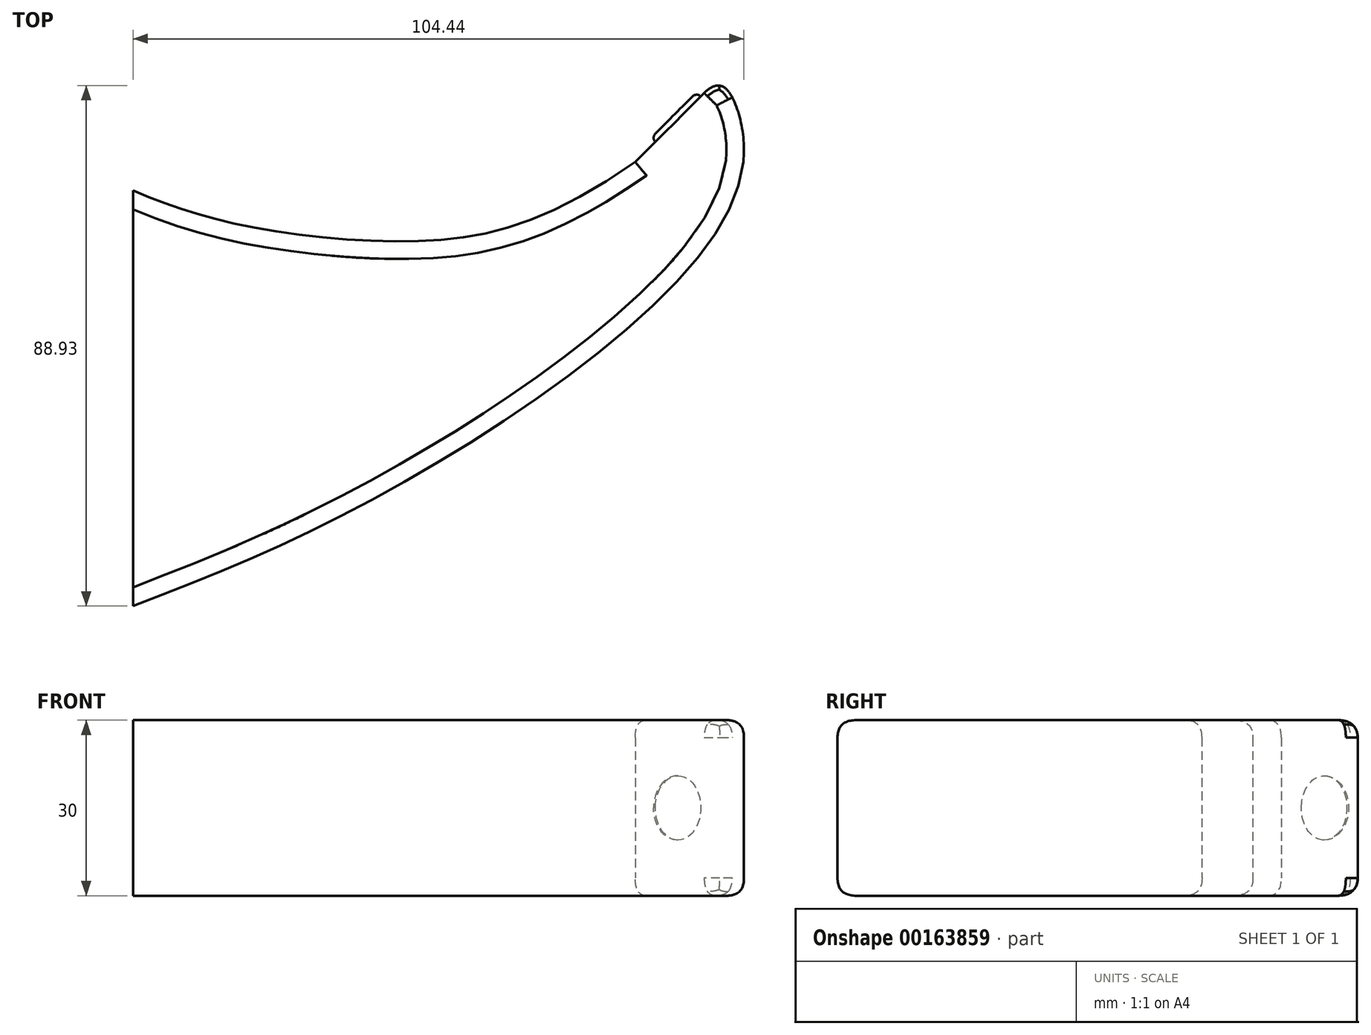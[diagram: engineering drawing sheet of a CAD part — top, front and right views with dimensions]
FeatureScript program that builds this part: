
annotation { "Feature Type Name" : "Feature", "Feature Type Description" : "" }
export const myFeature = defineFeature(function(context is Context, id is Id, definition is map)
    precondition{}
    {
        {
            var Q0;
            Q0=qCreatedBy(makeId("Top.planeOp"),FACE);
            var sketch = newSketch(context, id + "F0", { "sketchPlane" : qUnion([Q0])});
            skLineSegment(sketch, "E0", {"start": v(20.08, 24.8) * mm, "end": v(34.22, 38.94) * mm});
            skLineSegment(sketch, "E1", {"start": v(20.08, 24.8) * mm, "end": v(38.55, 24.8) * mm});
            skLineSegment(sketch, "E2", {"start": v(-65.78, -51.06) * mm, "end": v(-65.78, 48.94) * mm});
            skLineSegment(sketch, "E3", {"start": v(-65.78, -26.25) * mm, "end": v(-65.78, 19.94) * mm});
            skFitSpline(sketch, "E4", {"points": [v(-65.78, 19.94) * mm, v(-48.1, 14.22) * mm, v(-16.48, 11.31) * mm, v(20.08, 24.8) * mm], "startDerivative": vector(62.46, -26.54) * mm, "endDerivative": vector(118.27, 81.8) * mm});
            skFitSpline(sketch, "E5", {"points": [v(-65.78, -51.06) * mm, v(-27.67, -34.37) * mm, v(20.08, -2.5) * mm, v(38.55, 24.8) * mm, v(34.22, 38.94) * mm], "startDerivative": vector(142.55, 54.06) * mm, "endDerivative": vector(-50.17, 36.42) * mm});
            skLineSegment(sketch, "E6", {"start": v(34.22, 38.94) * mm, "end": v(-65.78, 38.94) * mm});
            skSolve(sketch);
        }
        {
            var Q0;
            {var subQ4=sQuery(id+"F0.wireOp",EDGE,"E1");Q0=makeQuery(id+"F0.imprint","IMPRINT",FACE,{"disambiguationData":[TD([[makeQuery(id+"F0.imprint","IMPRINT",EDGE,{"derivedFrom":subQ4}),-1.0]])]});}
            var Q1;
            {var subQ0=sQuery(id+"F0.wireOp",EDGE,"E0");Q1=makeQuery(id+"F0.imprint","IMPRINT",FACE,{"disambiguationData":[TD([[makeQuery(id+"F0.imprint","IMPRINT",EDGE,{"derivedFrom":subQ0}),-1.0]])]});}
            extrude(context, id + "F1", {"entities" : qUnion([Q0, Q1]), "endBound" : BoundingType.SYMMETRIC, "depth" : 30 * mm});
        }
        {
            var Q0;
            Q0=makeQuery(id+"F1.opExtrude","SWEPT_FACE",FACE,{"disambiguationData":[OSD([sQuery(id+"F0.wireOp",EDGE,"E0")])]});
            var sketch = newSketch(context, id + "F2", { "sketchPlane" : qUnion([Q0])});
            skCircle(sketch, "E7", {"center": v(-42.08, 0) * mm, "radius": 5.5 * mm});
            skSolve(sketch);
        }
        {
            var Q0;
            Q0=makeQuery(id+"F2.imprint","IMPRINT",FACE,{"disambiguationData":[TD([[makeQuery(id+"F2.imprint","IMPRINT",EDGE,{"derivedFrom":sQuery(id+"F2.wireOp",EDGE,"E7")}),1.0]])]});
            extrude(context, id + "F3", {"entities" : qUnion([Q0]), "operationType" : NewBodyOperationType.ADD, "depth" : 1 * mm});
        }
        {
            var Q0;
            Q0=makeQuery(id+"F3.opExtrude","CAP_FACE",FACE,{"disambiguationData":[OSD([sQuery(id+"F2.wireOp",EDGE,"E7")])],"isStart":false});
            fillet(context, id + "F4", {"entities" : qUnion([Q0]), "radius" : 1 * mm, "tangentPropagation" : true, "allowEdgeOverflow" : false});
        }
        {
            var Q0;
            Q0=makeQuery(id+"F1.opExtrude","SWEPT_EDGE",EDGE,{"disambiguationData":[OSD([sQuery(id+"F0.wireOp",EDGE,"E0"),sQuery(id+"F0.wireOp",EDGE,"E5"),sQuery(id+"F0.wireOp",EDGE,"E6")])]});
            var Q1;
            Q1=makeQuery(id+"F1.opExtrude","CAP_EDGE",EDGE,{"disambiguationData":[OSD([sQuery(id+"F0.wireOp",EDGE,"E5")])],"isStart":true});
            var Q2;
            Q2=makeQuery(id+"F1.opExtrude","CAP_EDGE",EDGE,{"disambiguationData":[OSD([sQuery(id+"F0.wireOp",EDGE,"E0")])],"isStart":true});
            var Q3;
            Q3=makeQuery(id+"F1.opExtrude","CAP_EDGE",EDGE,{"disambiguationData":[OSD([sQuery(id+"F0.wireOp",EDGE,"E4")])],"isStart":true});
            var Q4;
            Q4=makeQuery(id+"F1.opExtrude","CAP_EDGE",EDGE,{"disambiguationData":[OSD([sQuery(id+"F0.wireOp",EDGE,"E4")])],"isStart":false});
            var Q5;
            Q5=makeQuery(id+"F1.opExtrude","CAP_EDGE",EDGE,{"disambiguationData":[OSD([sQuery(id+"F0.wireOp",EDGE,"E5")])],"isStart":false});
            var Q6;
            Q6=makeQuery(id+"F1.opExtrude","CAP_EDGE",EDGE,{"disambiguationData":[OSD([sQuery(id+"F0.wireOp",EDGE,"E0")])],"isStart":false});
            fillet(context, id + "F5", {"entities" : qUnion([Q0, Q1, Q2, Q3, Q4, Q5, Q6]), "radius" : 3 * mm, "tangentPropagation" : true, "rho" : 0.5, "crossSection" : FilletCrossSection.CONIC, "allowEdgeOverflow" : false});
        }
    });
